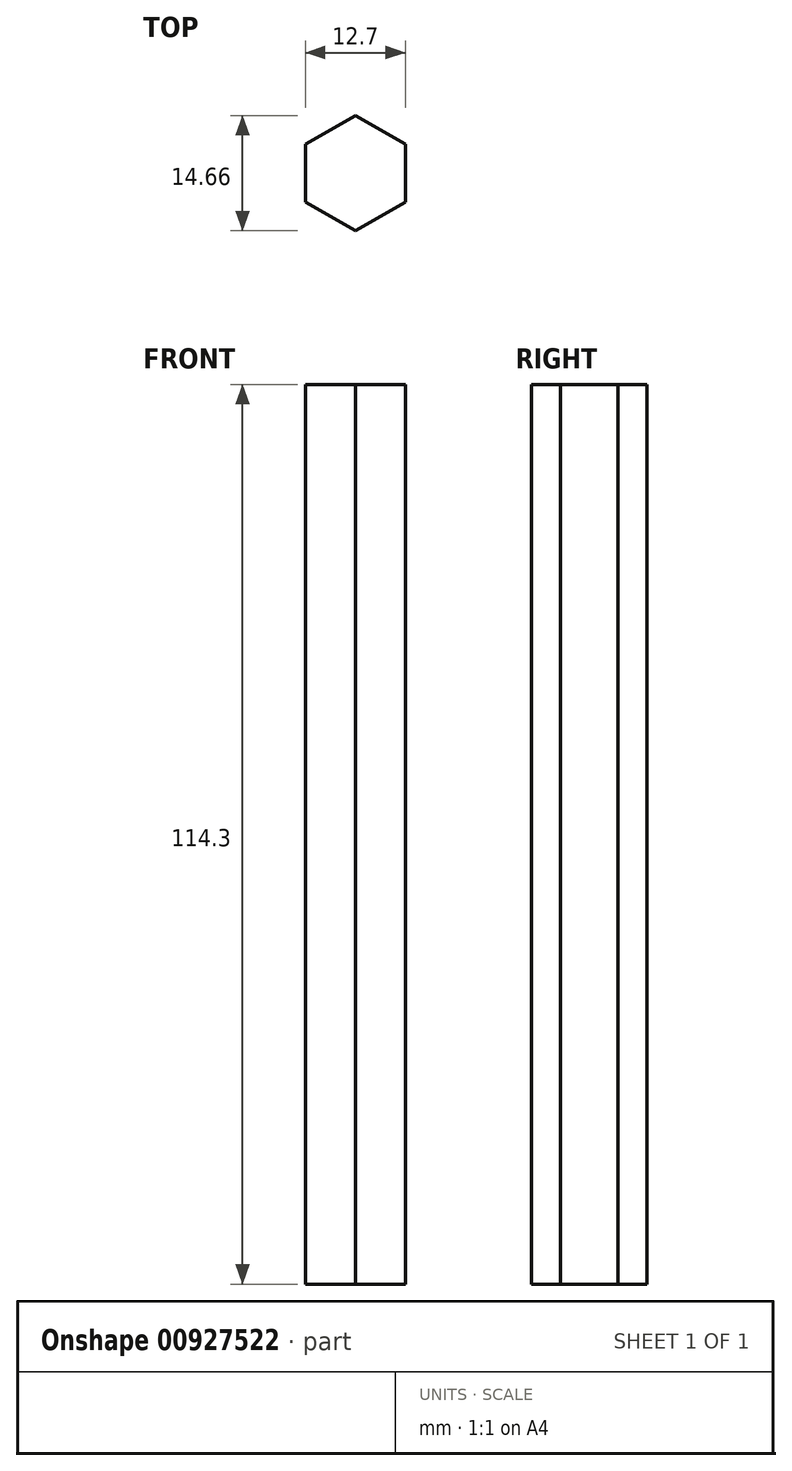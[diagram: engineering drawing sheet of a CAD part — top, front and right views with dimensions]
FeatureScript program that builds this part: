
annotation { "Feature Type Name" : "Feature", "Feature Type Description" : "" }
export const myFeature = defineFeature(function(context is Context, id is Id, definition is map)
    precondition{}
    {
        {
            var Q0;
            Q0=qCreatedBy(makeId("Top.planeOp"),FACE);
            var sketch = newSketch(context, id + "F0", { "sketchPlane" : qUnion([Q0])});
            skCircle(sketch, "E0.cCircle", {"center": v(0, 0) * mm, "radius": 6.35 * mm, "construction": true});
            skLineSegment(sketch, "E0.0", {"start": v(0, 7.33) * mm, "end": v(6.35, 3.67) * mm});
            skLineSegment(sketch, "E0.1", {"start": v(6.35, 3.67) * mm, "end": v(6.35, -3.67) * mm});
            skLineSegment(sketch, "E0.2", {"start": v(6.35, -3.67) * mm, "end": v(0, -7.33) * mm});
            skLineSegment(sketch, "E0.3", {"start": v(0, -7.33) * mm, "end": v(-6.35, -3.67) * mm});
            skLineSegment(sketch, "E0.4", {"start": v(-6.35, -3.67) * mm, "end": v(-6.35, 3.67) * mm});
            skLineSegment(sketch, "E0.5", {"start": v(-6.35, 3.67) * mm, "end": v(0, 7.33) * mm});
            skPoint(sketch, "E0.0.midPoint", {"position": v(3.17, 5.5) * mm});
            skSolve(sketch);
        }
        {
            var Q0;
            Q0 = qSketchRegion(id + "F0", true);
            extrude(context, id + "F1", {"entities" : qUnion([Q0]), "depth" : 114.3 * mm, "offsetDistance" : 25.4 * mm});
        }
    });
